AUTODESK INVENTOR PART (.ipt)
format: ipt  version: 2015 SP1 (Build 190203100, 203)  size: 84,992 bytes
history: native  units: mm
features: other x4, sketch x4
ambient origin geometry x8: Origin, YZ Plane, XZ Plane, XY Plane, X Axis, Y Axis, Z Axis, Center Point
bodies: Body1 (feature_tree)
feature tree (8):
  other  "brazo_botella.ipt"
  other  "Sólido1::brazo_botella.ipt"
  other  "OperaciónIdentificador1"
  sketch  "Boceto1"  dims[d0=10.0mm]
  sketch  "Boceto2"
  sketch  "Boceto3"
  sketch  "Boceto4"
  other  "Sólido1"
